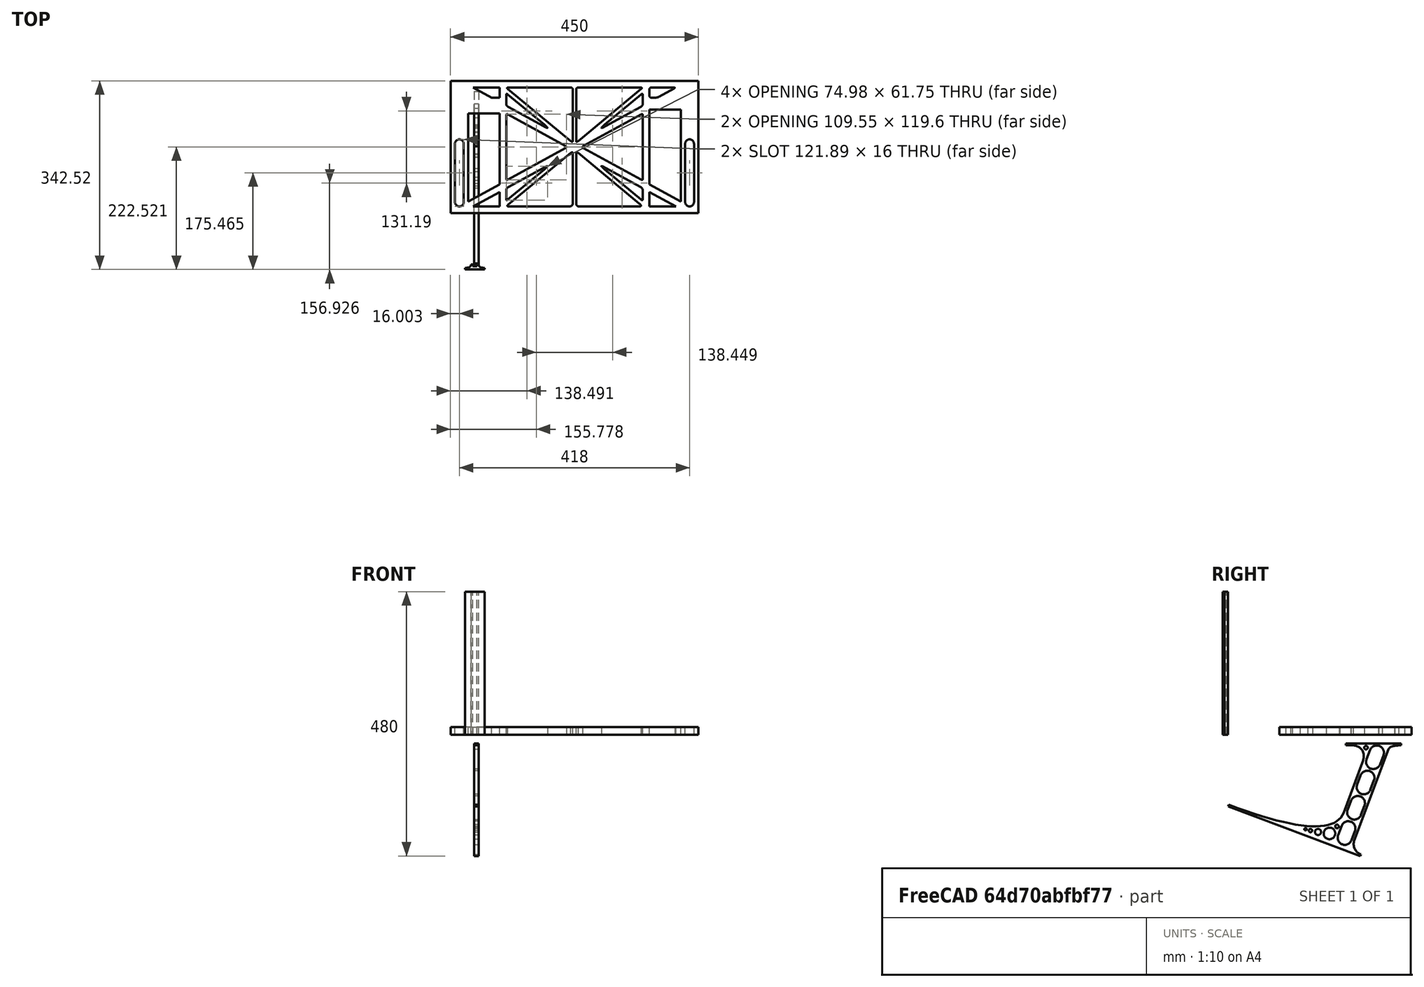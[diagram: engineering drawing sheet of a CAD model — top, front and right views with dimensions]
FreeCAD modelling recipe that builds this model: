
FCSTD DOCUMENT  (FreeCAD 0.19R0.19.2)
Label: laptopStand101
License: All rights reserved
LicenseURL: http://en.wikipedia.org/wiki/All_rights_reserved
objects: Sketcher::SketchObject×3, Part::Extrusion×3
note: 6 computed .brp shape members not serialized (recipe doc carries the construction recipe); baked Part::Feature solids carry a one-line shape summary decoded from their .brp

FEATURE [Sketcher::SketchObject] Sketch
  FullyConstrained = false
  sketch-geometry (276):
    g0: LineSegment StartX=-10.9272 StartY=-82.7794 StartZ=0 EndX=46.0728 EndY=-51.4823 EndZ=0
    g1: LineSegment StartX=366.073 StartY=-91.7794 StartZ=0 EndX=318.073 EndY=-65.424 EndZ=0
    g2: LineSegment StartX=-10.9272 StartY=77.3346 StartZ=0 EndX=-10.9272 EndY=-82.7794 EndZ=0
    g3: LineSegment StartX=375.073 StartY=-82.7794 StartZ=0 EndX=375.073 EndY=83.9235 EndZ=0
    g4: LineSegment StartX=-1.92719 StartY=-91.7794 StartZ=0 EndX=46.0728 EndY=-91.7794 EndZ=0
    g5: LineSegment StartX=318.073 StartY=83.9235 StartZ=0 EndX=318.073 EndY=-51.4823 EndZ=0
    g6: LineSegment StartX=318.073 StartY=-51.4823 StartZ=0 EndX=375.073 EndY=-82.7794 EndZ=0
    g7: LineSegment StartX=318.073 StartY=-65.424 StartZ=0 EndX=318.073 EndY=-91.7794 EndZ=0
    g8: LineSegment StartX=318.073 StartY=-91.7794 StartZ=0 EndX=366.073 EndY=-91.7794 EndZ=0
    g9: LineSegment StartX=46.0728 StartY=-65.424 StartZ=0 EndX=-1.92719 EndY=-91.7794 EndZ=0
    g10: LineSegment StartX=46.0728 StartY=-65.424 StartZ=0 EndX=46.0728 EndY=-91.7794 EndZ=0
    g11: LineSegment StartX=46.0728 StartY=77.3346 StartZ=0 EndX=46.0728 EndY=-51.4823 EndZ=0
    g12: LineSegment StartX=-42.9272 StartY=136.221 StartZ=0 EndX=-42.9272 EndY=-103.779 EndZ=0
    g13: LineSegment StartX=407.073 StartY=136.221 StartZ=0 EndX=407.073 EndY=-103.779 EndZ=0
    g14: ArcOfCircle CenterX=-26.9272 CenterY=22.1087 CenterZ=0 NormalX=0 NormalY=0 NormalZ=1 AngleXU=0 Radius=8 StartAngle=1e-16 EndAngle=3.14159
    g15: ArcOfCircle CenterX=-26.9272 CenterY=-83.7794 CenterZ=0 NormalX=0 NormalY=0 NormalZ=1 AngleXU=0 Radius=8 StartAngle=3.14159 EndAngle=6.28319
    g16: LineSegment StartX=-34.9272 StartY=22.1087 StartZ=0 EndX=-34.9272 EndY=-83.7794 EndZ=0
    g17: LineSegment StartX=-18.9272 StartY=22.1087 StartZ=0 EndX=-18.9272 EndY=-83.7794 EndZ=0
    g18: ArcOfCircle CenterX=391.073 CenterY=22.1087 CenterZ=0 NormalX=0 NormalY=0 NormalZ=1 AngleXU=0 Radius=8 StartAngle=-4.4e-15 EndAngle=3.14159
    g19: LineSegment StartX=399.073 StartY=22.1087 StartZ=0 EndX=399.073 EndY=-83.7794 EndZ=0
    g20: LineSegment StartX=383.073 StartY=22.1087 StartZ=0 EndX=383.073 EndY=-83.7794 EndZ=0
    g21: ArcOfCircle CenterX=391.073 CenterY=-83.7794 CenterZ=0 NormalX=0 NormalY=0 NormalZ=1 AngleXU=0 Radius=8 StartAngle=3.14159 EndAngle=6.28319
    g22: Circle CenterX=175.022 CenterY=27.0628 CenterZ=0 NormalX=0 NormalY=0 NormalZ=1 AngleXU=0 Radius=1
    g23: Circle CenterX=179.022 CenterY=24.8665 CenterZ=0 NormalX=0 NormalY=0 NormalZ=1 AngleXU=0 Radius=1
    g24: Circle CenterX=179.022 CenterY=27.0628 CenterZ=0 NormalX=0 NormalY=0 NormalZ=1 AngleXU=0 Radius=1
    g25: BSplineCurve PolesCount=3 KnotsCount=2 Degree=2 IsPeriodic=0
    g26: GeomPoint X=175.022 Y=27.0628 Z=0
    g27: GeomPoint X=179.022 Y=27.0628 Z=0
    g28: Circle CenterX=189.124 CenterY=27.0628 CenterZ=0 NormalX=0 NormalY=0 NormalZ=1 AngleXU=0 Radius=1
    g29: Circle CenterX=185.124 CenterY=24.8665 CenterZ=0 NormalX=0 NormalY=0 NormalZ=1 AngleXU=0 Radius=1
    g30: Circle CenterX=185.124 CenterY=27.0628 CenterZ=0 NormalX=0 NormalY=0 NormalZ=1 AngleXU=0 Radius=1
    g31: BSplineCurve PolesCount=3 KnotsCount=2 Degree=2 IsPeriodic=0
    g32: GeomPoint X=189.124 Y=27.0628 Z=0
    g33: GeomPoint X=185.124 Y=27.0628 Z=0
    g34: Circle CenterX=175.022 CenterY=5.37834 CenterZ=0 NormalX=0 NormalY=0 NormalZ=1 AngleXU=0 Radius=1
    g35: Circle CenterX=179.022 CenterY=7.57463 CenterZ=0 NormalX=0 NormalY=0 NormalZ=1 AngleXU=0 Radius=1
    g36: Circle CenterX=179.022 CenterY=5.34704 CenterZ=0 NormalX=0 NormalY=0 NormalZ=1 AngleXU=0 Radius=1
    g37: BSplineCurve PolesCount=3 KnotsCount=2 Degree=2 IsPeriodic=0
    g38: GeomPoint X=175.022 Y=5.37834 Z=0
    g39: GeomPoint X=179.022 Y=5.34704 Z=0
    g40: Circle CenterX=189.124 CenterY=5.37834 CenterZ=0 NormalX=0 NormalY=0 NormalZ=1 AngleXU=0 Radius=1
    g41: Circle CenterX=185.124 CenterY=7.57463 CenterZ=0 NormalX=0 NormalY=0 NormalZ=1 AngleXU=0 Radius=1
    g42: Circle CenterX=185.124 CenterY=5.34704 CenterZ=0 NormalX=0 NormalY=0 NormalZ=1 AngleXU=0 Radius=1
    g43: BSplineCurve PolesCount=3 KnotsCount=2 Degree=2 IsPeriodic=0
    g44: GeomPoint X=189.124 Y=5.37834 Z=0
    g45: GeomPoint X=185.124 Y=5.34704 Z=0
    g46: Circle CenterX=165.871 CenterY=18.1458 CenterZ=0 NormalX=0 NormalY=0 NormalZ=1 AngleXU=0 Radius=1
    g47: Circle CenterX=169.377 CenterY=16.2206 CenterZ=0 NormalX=0 NormalY=0 NormalZ=1 AngleXU=0 Radius=1
    g48: Circle CenterX=165.871 CenterY=14.2954 CenterZ=0 NormalX=0 NormalY=0 NormalZ=1 AngleXU=0 Radius=1
    g49: BSplineCurve PolesCount=3 KnotsCount=2 Degree=2 IsPeriodic=0
    g50: GeomPoint X=165.871 Y=18.1458 Z=0
    g51: GeomPoint X=165.871 Y=14.2954 Z=0
    g52: Circle CenterX=198.275 CenterY=18.1458 CenterZ=0 NormalX=0 NormalY=0 NormalZ=1 AngleXU=0 Radius=1
    g53: Circle CenterX=194.768 CenterY=16.2206 CenterZ=0 NormalX=0 NormalY=0 NormalZ=1 AngleXU=0 Radius=1
    g54: Circle CenterX=198.275 CenterY=14.2954 CenterZ=0 NormalX=0 NormalY=0 NormalZ=1 AngleXU=0 Radius=1
    g55: BSplineCurve PolesCount=3 KnotsCount=2 Degree=2 IsPeriodic=0
    g56: GeomPoint X=198.275 Y=18.1458 Z=0
    g57: GeomPoint X=198.275 Y=14.2954 Z=0
    g58: LineSegment StartX=407.073 StartY=-103.779 StartZ=0 EndX=-42.9272 EndY=-103.779 EndZ=0
    g59: LineSegment StartX=407.073 StartY=136.221 StartZ=0 EndX=-42.9272 EndY=136.221 EndZ=0
    g60: LineSegment StartX=46.0728 StartY=77.3346 StartZ=0 EndX=-10.9272 EndY=77.3346 EndZ=0
    g61: LineSegment StartX=46.0728 StartY=105.865 StartZ=0 EndX=31.5028 EndY=105.865 EndZ=0
    g62: LineSegment StartX=46.0728 StartY=124.221 StartZ=0 EndX=46.0728 EndY=105.865 EndZ=0
    g63: LineSegment StartX=-1.92719 StartY=124.221 StartZ=0 EndX=31.5028 EndY=105.865 EndZ=0
    g64: LineSegment StartX=46.0728 StartY=124.221 StartZ=0 EndX=-1.92719 EndY=124.221 EndZ=0
    g65: LineSegment StartX=318.073 StartY=83.9235 StartZ=0 EndX=375.073 EndY=83.9235 EndZ=0
    g66: Circle CenterX=125.607 CenterY=54.1951 CenterZ=0 NormalX=0 NormalY=0 NormalZ=1 AngleXU=0 Radius=1
    g67: Circle CenterX=139.632 CenterY=46.4944 CenterZ=0 NormalX=0 NormalY=0 NormalZ=1 AngleXU=0 Radius=1
    g68: Circle CenterX=127.326 CenterY=56.7187 CenterZ=0 NormalX=0 NormalY=0 NormalZ=1 AngleXU=0 Radius=1
    g69: BSplineCurve PolesCount=3 KnotsCount=2 Degree=2 IsPeriodic=0
    g70: GeomPoint X=125.607 Y=54.1951 Z=0
    g71: GeomPoint X=127.326 Y=56.7187 Z=0
    g72: Circle CenterX=236.821 CenterY=56.7187 CenterZ=0 NormalX=0 NormalY=0 NormalZ=1 AngleXU=0 Radius=1
    g73: Circle CenterX=224.513 CenterY=46.4944 CenterZ=0 NormalX=0 NormalY=0 NormalZ=1 AngleXU=0 Radius=1
    g74: Circle CenterX=238.538 CenterY=54.1951 CenterZ=0 NormalX=0 NormalY=0 NormalZ=1 AngleXU=0 Radius=1
    g75: BSplineCurve PolesCount=3 KnotsCount=2 Degree=2 IsPeriodic=0
    g76: GeomPoint X=236.821 Y=56.7187 Z=0
    g77: GeomPoint X=238.538 Y=54.1951 Z=0
    g78: Circle CenterX=238.538 CenterY=-21.7539 CenterZ=0 NormalX=0 NormalY=0 NormalZ=1 AngleXU=0 Radius=1
    g79: Circle CenterX=224.513 CenterY=-14.0532 CenterZ=0 NormalX=0 NormalY=0 NormalZ=1 AngleXU=0 Radius=1
    g80: Circle CenterX=236.821 CenterY=-24.2775 CenterZ=0 NormalX=0 NormalY=0 NormalZ=1 AngleXU=0 Radius=1
    g81: BSplineCurve PolesCount=3 KnotsCount=2 Degree=2 IsPeriodic=0
    g82: GeomPoint X=238.538 Y=-21.7539 Z=0
    g83: GeomPoint X=236.821 Y=-24.2775 Z=0
    g84: Circle CenterX=125.607 CenterY=-21.7539 CenterZ=0 NormalX=0 NormalY=0 NormalZ=1 AngleXU=0 Radius=1
    g85: Circle CenterX=139.632 CenterY=-14.0532 CenterZ=0 NormalX=0 NormalY=0 NormalZ=1 AngleXU=0 Radius=1
    g86: Circle CenterX=127.325 CenterY=-24.2775 CenterZ=0 NormalX=0 NormalY=0 NormalZ=1 AngleXU=0 Radius=1
    g87: BSplineCurve PolesCount=3 KnotsCount=2 Degree=2 IsPeriodic=0
    g88: GeomPoint X=125.607 Y=-21.7539 Z=0
    g89: GeomPoint X=127.325 Y=-24.2775 Z=0
    g90: Circle CenterX=302.996 CenterY=111.695 CenterZ=0 NormalX=0 NormalY=0 NormalZ=1 AngleXU=0 Radius=1
    g91: Circle CenterX=306.073 CenterY=114.251 CenterZ=0 NormalX=0 NormalY=0 NormalZ=1 AngleXU=0 Radius=1
    g92: Circle CenterX=306.073 CenterY=110.251 CenterZ=0 NormalX=0 NormalY=0 NormalZ=1 AngleXU=0 Radius=1
    g93: BSplineCurve PolesCount=3 KnotsCount=2 Degree=2 IsPeriodic=0
    g94: GeomPoint X=302.996 Y=111.695 Z=0
    g95: GeomPoint X=306.073 Y=110.251 Z=0
    g96: Circle CenterX=306.073 CenterY=95.2763 CenterZ=0 NormalX=0 NormalY=0 NormalZ=1 AngleXU=0 Radius=1
    g97: Circle CenterX=306.073 CenterY=91.2763 CenterZ=0 NormalX=0 NormalY=0 NormalZ=1 AngleXU=0 Radius=1
    g98: Circle CenterX=302.567 CenterY=89.3511 CenterZ=0 NormalX=0 NormalY=0 NormalZ=1 AngleXU=0 Radius=1
    g99: BSplineCurve PolesCount=3 KnotsCount=2 Degree=2 IsPeriodic=0
    g100: GeomPoint X=306.073 Y=95.2763 Z=0
    g101: GeomPoint X=302.567 Y=89.3511 Z=0
    g102: LineSegment StartX=306.073 StartY=110.251 StartZ=0 EndX=306.073 EndY=95.2763 EndZ=0
    g103: LineSegment StartX=302.996 StartY=111.695 StartZ=0 EndX=236.821 EndY=56.7187 EndZ=0
    g104: LineSegment StartX=238.538 StartY=54.1951 StartZ=0 EndX=302.567 EndY=89.3511 EndZ=0
    g105: Circle CenterX=61.1496 CenterY=111.695 CenterZ=0 NormalX=0 NormalY=0 NormalZ=1 AngleXU=0 Radius=1
    g106: Circle CenterX=58.0728 CenterY=114.251 CenterZ=0 NormalX=0 NormalY=0 NormalZ=1 AngleXU=0 Radius=1
    g107: Circle CenterX=58.0728 CenterY=110.251 CenterZ=0 NormalX=0 NormalY=0 NormalZ=1 AngleXU=0 Radius=1
    g108: BSplineCurve PolesCount=3 KnotsCount=2 Degree=2 IsPeriodic=0
    g109: GeomPoint X=61.1496 Y=111.695 Z=0
    g110: GeomPoint X=58.0728 Y=110.251 Z=0
    g111: Circle CenterX=61.5791 CenterY=89.3511 CenterZ=0 NormalX=0 NormalY=0 NormalZ=1 AngleXU=0 Radius=1
    g112: Circle CenterX=58.0728 CenterY=91.2763 CenterZ=0 NormalX=0 NormalY=0 NormalZ=1 AngleXU=0 Radius=1
    g113: Circle CenterX=58.0728 CenterY=95.2763 CenterZ=0 NormalX=0 NormalY=0 NormalZ=1 AngleXU=0 Radius=1
    g114: BSplineCurve PolesCount=3 KnotsCount=2 Degree=2 IsPeriodic=0
    g115: GeomPoint X=61.5791 Y=89.3511 Z=0
    g116: GeomPoint X=58.0728 Y=95.2763 Z=0
    g117: LineSegment StartX=58.0728 StartY=110.251 StartZ=0 EndX=58.0728 EndY=95.2763 EndZ=0
    g118: LineSegment StartX=61.1496 StartY=111.695 StartZ=0 EndX=127.326 EndY=56.7187 EndZ=0
    g119: LineSegment StartX=125.607 StartY=54.1951 StartZ=0 EndX=61.5791 EndY=89.3511 EndZ=0
    g120: Circle CenterX=61.5791 CenterY=-56.9099 CenterZ=0 NormalX=0 NormalY=0 NormalZ=1 AngleXU=0 Radius=1
    g121: Circle CenterX=58.0728 CenterY=-58.8351 CenterZ=0 NormalX=0 NormalY=0 NormalZ=1 AngleXU=0 Radius=1
    g122: Circle CenterX=58.0728 CenterY=-62.8351 CenterZ=0 NormalX=0 NormalY=0 NormalZ=1 AngleXU=0 Radius=1
    g123: BSplineCurve PolesCount=3 KnotsCount=2 Degree=2 IsPeriodic=0
    g124: GeomPoint X=61.5791 Y=-56.9099 Z=0
    g125: GeomPoint X=58.0728 Y=-62.8351 Z=0
    g126: Circle CenterX=58.0728 CenterY=-77.8102 CenterZ=0 NormalX=0 NormalY=0 NormalZ=1 AngleXU=0 Radius=1
    g127: Circle CenterX=58.0728 CenterY=-81.8102 CenterZ=0 NormalX=0 NormalY=0 NormalZ=1 AngleXU=0 Radius=1
    g128: Circle CenterX=61.1496 CenterY=-79.2541 CenterZ=0 NormalX=0 NormalY=0 NormalZ=1 AngleXU=0 Radius=1
    g129: BSplineCurve PolesCount=3 KnotsCount=2 Degree=2 IsPeriodic=0
    g130: GeomPoint X=58.0728 Y=-77.8102 Z=0
    g131: GeomPoint X=61.1496 Y=-79.2541 Z=0
    g132: LineSegment StartX=58.0728 StartY=-62.8351 StartZ=0 EndX=58.0728 EndY=-77.8102 EndZ=0
    g133: LineSegment StartX=61.1496 StartY=-79.2541 StartZ=0 EndX=127.325 EndY=-24.2775 EndZ=0
    g134: LineSegment StartX=125.607 StartY=-21.7539 StartZ=0 EndX=61.5791 EndY=-56.9099 EndZ=0
    g135: Circle CenterX=302.567 CenterY=-56.9099 CenterZ=0 NormalX=0 NormalY=0 NormalZ=1 AngleXU=0 Radius=1
    g136: Circle CenterX=306.073 CenterY=-58.8351 CenterZ=0 NormalX=0 NormalY=0 NormalZ=1 AngleXU=0 Radius=1
    g137: Circle CenterX=306.073 CenterY=-62.8351 CenterZ=0 NormalX=0 NormalY=0 NormalZ=1 AngleXU=0 Radius=1
    g138: BSplineCurve PolesCount=3 KnotsCount=2 Degree=2 IsPeriodic=0
    g139: GeomPoint X=302.567 Y=-56.9099 Z=0
    g140: GeomPoint X=306.073 Y=-62.8351 Z=0
    g141: Circle CenterX=302.996 CenterY=-79.2541 CenterZ=0 NormalX=0 NormalY=0 NormalZ=1 AngleXU=0 Radius=1
    g142: Circle CenterX=306.073 CenterY=-81.8102 CenterZ=0 NormalX=0 NormalY=0 NormalZ=1 AngleXU=0 Radius=1
    g143: Circle CenterX=306.073 CenterY=-77.8102 CenterZ=0 NormalX=0 NormalY=0 NormalZ=1 AngleXU=0 Radius=1
    g144: BSplineCurve PolesCount=3 KnotsCount=2 Degree=2 IsPeriodic=0
    g145: GeomPoint X=302.996 Y=-79.2541 Z=0
    g146: GeomPoint X=306.073 Y=-77.8102 Z=0
    g147: LineSegment StartX=306.073 StartY=-62.8351 StartZ=0 EndX=306.073 EndY=-77.8102 EndZ=0
    g148: LineSegment StartX=302.996 StartY=-79.2541 StartZ=0 EndX=236.821 EndY=-24.2775 EndZ=0
    g149: LineSegment StartX=238.538 StartY=-21.7539 StartZ=0 EndX=302.567 EndY=-56.9099 EndZ=0
    g150: Circle CenterX=61.6457 CenterY=-88.8112 CenterZ=0 NormalX=0 NormalY=0 NormalZ=1 AngleXU=0 Radius=1
    g151: Circle CenterX=58.0728 CenterY=-91.7794 CenterZ=0 NormalX=0 NormalY=0 NormalZ=1 AngleXU=0 Radius=1
    g152: Circle CenterX=63.9135 CenterY=-91.7794 CenterZ=0 NormalX=0 NormalY=0 NormalZ=1 AngleXU=0 Radius=1
    g153: BSplineCurve PolesCount=3 KnotsCount=2 Degree=2 IsPeriodic=0
    g154: GeomPoint X=61.6457 Y=-88.8112 Z=0
    g155: GeomPoint X=63.9135 Y=-91.7794 Z=0
    g156: Circle CenterX=179.022 CenterY=-85.8163 CenterZ=0 NormalX=0 NormalY=0 NormalZ=1 AngleXU=0 Radius=1
    g157: Circle CenterX=179.022 CenterY=-91.7794 CenterZ=0 NormalX=0 NormalY=0 NormalZ=1 AngleXU=0 Radius=1
    g158: Circle CenterX=171.895 CenterY=-91.7794 CenterZ=0 NormalX=0 NormalY=0 NormalZ=1 AngleXU=0 Radius=1
    g159: BSplineCurve PolesCount=3 KnotsCount=2 Degree=2 IsPeriodic=0
    g160: GeomPoint X=179.022 Y=-85.8163 Z=0
    g161: GeomPoint X=171.895 Y=-91.7794 Z=0
    g162: Circle CenterX=185.124 CenterY=-86.2028 CenterZ=0 NormalX=0 NormalY=0 NormalZ=1 AngleXU=0 Radius=1
    g163: Circle CenterX=185.124 CenterY=-91.7794 CenterZ=0 NormalX=0 NormalY=0 NormalZ=1 AngleXU=0 Radius=1
    g164: Circle CenterX=191.747 CenterY=-91.7794 CenterZ=0 NormalX=0 NormalY=0 NormalZ=1 AngleXU=0 Radius=1
    g165: BSplineCurve PolesCount=3 KnotsCount=2 Degree=2 IsPeriodic=0
    g166: GeomPoint X=185.124 Y=-86.2028 Z=0
    g167: GeomPoint X=191.747 Y=-91.7794 Z=0
    g168: Circle CenterX=299.888 CenterY=-86.6413 CenterZ=0 NormalX=0 NormalY=0 NormalZ=1 AngleXU=0 Radius=1
    g169: Circle CenterX=306.073 CenterY=-91.7794 CenterZ=0 NormalX=0 NormalY=0 NormalZ=1 AngleXU=0 Radius=1
    g170: Circle CenterX=298.776 CenterY=-91.7794 CenterZ=0 NormalX=0 NormalY=0 NormalZ=1 AngleXU=0 Radius=1
    g171: BSplineCurve PolesCount=3 KnotsCount=2 Degree=2 IsPeriodic=0
    g172: GeomPoint X=299.888 Y=-86.6413 Z=0
    g173: GeomPoint X=298.776 Y=-91.7794 Z=0
    g174: LineSegment StartX=189.124 StartY=5.37834 StartZ=0 EndX=299.888 EndY=-86.6413 EndZ=0
    g175: LineSegment StartX=298.776 StartY=-91.7794 StartZ=0 EndX=191.747 EndY=-91.7794 EndZ=0
    g176: LineSegment StartX=185.124 StartY=-86.2028 StartZ=0 EndX=185.124 EndY=5.34704 EndZ=0
    g177: LineSegment StartX=179.022 StartY=5.34704 StartZ=0 EndX=179.022 EndY=-85.8163 EndZ=0
    g178: LineSegment StartX=171.895 StartY=-91.7794 StartZ=0 EndX=63.9135 EndY=-91.7794 EndZ=0
    g179: LineSegment StartX=61.6457 StartY=-88.8112 StartZ=0 EndX=175.022 EndY=5.37834 EndZ=0
    g180: Circle CenterX=302.073 CenterY=124.221 CenterZ=0 NormalX=0 NormalY=0 NormalZ=1 AngleXU=0 Radius=1
    g181: Circle CenterX=306.073 CenterY=124.221 CenterZ=0 NormalX=0 NormalY=0 NormalZ=1 AngleXU=0 Radius=1
    g182: Circle CenterX=302.996 CenterY=121.665 CenterZ=0 NormalX=0 NormalY=0 NormalZ=1 AngleXU=0 Radius=1
    g183: BSplineCurve PolesCount=3 KnotsCount=2 Degree=2 IsPeriodic=0
    g184: GeomPoint X=302.073 Y=124.221 Z=0
    g185: GeomPoint X=302.996 Y=121.665 Z=0
    g186: Circle CenterX=189.124 CenterY=124.221 CenterZ=0 NormalX=0 NormalY=0 NormalZ=1 AngleXU=0 Radius=1
    g187: Circle CenterX=185.124 CenterY=124.221 CenterZ=0 NormalX=0 NormalY=0 NormalZ=1 AngleXU=0 Radius=1
    g188: Circle CenterX=185.124 CenterY=120.221 CenterZ=0 NormalX=0 NormalY=0 NormalZ=1 AngleXU=0 Radius=1
    g189: BSplineCurve PolesCount=3 KnotsCount=2 Degree=2 IsPeriodic=0
    g190: GeomPoint X=189.124 Y=124.221 Z=0
    g191: GeomPoint X=185.124 Y=120.221 Z=0
    g192: Circle CenterX=175.022 CenterY=124.221 CenterZ=0 NormalX=0 NormalY=0 NormalZ=1 AngleXU=0 Radius=1
    g193: Circle CenterX=179.022 CenterY=124.221 CenterZ=0 NormalX=0 NormalY=0 NormalZ=1 AngleXU=0 Radius=1
    g194: Circle CenterX=179.022 CenterY=120.221 CenterZ=0 NormalX=0 NormalY=0 NormalZ=1 AngleXU=0 Radius=1
    g195: BSplineCurve PolesCount=3 KnotsCount=2 Degree=2 IsPeriodic=0
    g196: GeomPoint X=175.022 Y=124.221 Z=0
    g197: GeomPoint X=179.022 Y=120.221 Z=0
    g198: Circle CenterX=62.0728 CenterY=124.221 CenterZ=0 NormalX=0 NormalY=0 NormalZ=1 AngleXU=0 Radius=1
    g199: Circle CenterX=58.0728 CenterY=124.221 CenterZ=0 NormalX=0 NormalY=0 NormalZ=1 AngleXU=0 Radius=1
    g200: Circle CenterX=61.1496 CenterY=121.665 CenterZ=0 NormalX=0 NormalY=0 NormalZ=1 AngleXU=0 Radius=1
    g201: BSplineCurve PolesCount=3 KnotsCount=2 Degree=2 IsPeriodic=0
    g202: GeomPoint X=62.0728 Y=124.221 Z=0
    g203: GeomPoint X=61.1496 Y=121.665 Z=0
    g204: LineSegment StartX=62.0728 StartY=124.221 StartZ=0 EndX=175.022 EndY=124.221 EndZ=0
    g205: LineSegment StartX=179.022 StartY=120.221 StartZ=0 EndX=179.022 EndY=27.0628 EndZ=0
    g206: LineSegment StartX=185.124 StartY=27.0628 StartZ=0 EndX=185.124 EndY=120.221 EndZ=0
    g207: LineSegment StartX=189.124 StartY=124.221 StartZ=0 EndX=302.073 EndY=124.221 EndZ=0
    g208: LineSegment StartX=302.996 StartY=121.665 StartZ=0 EndX=189.124 EndY=27.0628 EndZ=0
    g209: LineSegment StartX=175.022 StartY=27.0628 StartZ=0 EndX=61.1496 EndY=121.665 EndZ=0
    g210: Circle CenterX=61.5791 CenterY=75.4095 CenterZ=0 NormalX=0 NormalY=0 NormalZ=1 AngleXU=0 Radius=1
    g211: Circle CenterX=58.0728 CenterY=77.3346 CenterZ=0 NormalX=0 NormalY=0 NormalZ=1 AngleXU=0 Radius=1
    g212: Circle CenterX=58.0728 CenterY=73.3346 CenterZ=0 NormalX=0 NormalY=0 NormalZ=1 AngleXU=0 Radius=1
    g213: BSplineCurve PolesCount=3 KnotsCount=2 Degree=2 IsPeriodic=0
    g214: GeomPoint X=61.5791 Y=75.4095 Z=0
    g215: GeomPoint X=58.0728 Y=73.3346 Z=0
    g216: Circle CenterX=58.0728 CenterY=-40.8935 CenterZ=0 NormalX=0 NormalY=0 NormalZ=1 AngleXU=0 Radius=1
    g217: Circle CenterX=58.0728 CenterY=-44.8935 CenterZ=0 NormalX=0 NormalY=0 NormalZ=1 AngleXU=0 Radius=1
    g218: Circle CenterX=61.5791 CenterY=-42.9683 CenterZ=0 NormalX=0 NormalY=0 NormalZ=1 AngleXU=0 Radius=1
    g219: BSplineCurve PolesCount=3 KnotsCount=2 Degree=2 IsPeriodic=0
    g220: GeomPoint X=58.0728 Y=-40.8935 Z=0
    g221: GeomPoint X=61.5791 Y=-42.9683 Z=0
    g222: LineSegment StartX=61.5791 StartY=-42.9683 StartZ=0 EndX=165.871 EndY=14.2954 EndZ=0
    g223: LineSegment StartX=165.871 StartY=18.1458 StartZ=0 EndX=61.5791 EndY=75.4095 EndZ=0
    g224: LineSegment StartX=58.0728 StartY=73.3346 StartZ=0 EndX=58.0728 EndY=-40.8935 EndZ=0
    g225: Circle CenterX=302.567 CenterY=-42.9683 CenterZ=0 NormalX=0 NormalY=0 NormalZ=1 AngleXU=0 Radius=1
    g226: Circle CenterX=306.073 CenterY=-44.8935 CenterZ=0 NormalX=0 NormalY=0 NormalZ=1 AngleXU=0 Radius=1
    g227: Circle CenterX=306.073 CenterY=-40.8935 CenterZ=0 NormalX=0 NormalY=0 NormalZ=1 AngleXU=0 Radius=1
    g228: BSplineCurve PolesCount=3 KnotsCount=2 Degree=2 IsPeriodic=0
    g229: GeomPoint X=302.567 Y=-42.9683 Z=0
    g230: GeomPoint X=306.073 Y=-40.8935 Z=0
    g231: Circle CenterX=306.073 CenterY=73.3346 CenterZ=0 NormalX=0 NormalY=0 NormalZ=1 AngleXU=0 Radius=1
    g232: Circle CenterX=306.073 CenterY=77.3346 CenterZ=0 NormalX=0 NormalY=0 NormalZ=1 AngleXU=0 Radius=1
    g233: Circle CenterX=302.567 CenterY=75.4095 CenterZ=0 NormalX=0 NormalY=0 NormalZ=1 AngleXU=0 Radius=1
    g234: BSplineCurve PolesCount=3 KnotsCount=2 Degree=2 IsPeriodic=0
    g235: GeomPoint X=306.073 Y=73.3346 Z=0
    g236: GeomPoint X=302.567 Y=75.4095 Z=0
    g237: LineSegment StartX=302.567 StartY=-42.9683 StartZ=0 EndX=198.275 EndY=14.2954 EndZ=0
    g238: LineSegment StartX=198.275 StartY=18.1458 StartZ=0 EndX=302.567 EndY=75.4095 EndZ=0
    g239: LineSegment StartX=306.073 StartY=73.3346 StartZ=0 EndX=306.073 EndY=-40.8935 EndZ=0
    g240: LineSegment StartX=322.073 StartY=105.865 StartZ=0 EndX=328.643 EndY=105.865 EndZ=0
    g241: LineSegment StartX=318.073 StartY=120.221 StartZ=0 EndX=318.073 EndY=109.865 EndZ=0
    g242: LineSegment StartX=336.157 StartY=107.779 StartZ=0 EndX=362.567 EndY=122.294 EndZ=0
    g243: Circle CenterX=362.073 CenterY=124.221 CenterZ=0 NormalX=0 NormalY=0 NormalZ=1 AngleXU=0 Radius=1
    g244: Circle CenterX=366.073 CenterY=124.221 CenterZ=0 NormalX=0 NormalY=0 NormalZ=1 AngleXU=0 Radius=1
    g245: Circle CenterX=362.567 CenterY=122.294 CenterZ=0 NormalX=0 NormalY=0 NormalZ=1 AngleXU=0 Radius=1
    g246: BSplineCurve PolesCount=3 KnotsCount=2 Degree=2 IsPeriodic=0
    g247: GeomPoint X=362.073 Y=124.221 Z=0
    g248: GeomPoint X=362.567 Y=122.294 Z=0
    g249: Circle CenterX=322.073 CenterY=124.221 CenterZ=0 NormalX=0 NormalY=0 NormalZ=1 AngleXU=0 Radius=1
    g250: Circle CenterX=318.073 CenterY=124.221 CenterZ=0 NormalX=0 NormalY=0 NormalZ=1 AngleXU=0 Radius=1
    g251: Circle CenterX=318.073 CenterY=120.221 CenterZ=0 NormalX=0 NormalY=0 NormalZ=1 AngleXU=0 Radius=1
    g252: BSplineCurve PolesCount=3 KnotsCount=2 Degree=2 IsPeriodic=0
    g253: GeomPoint X=322.073 Y=124.221 Z=0
    g254: GeomPoint X=318.073 Y=120.221 Z=0
    g255: Circle CenterX=322.073 CenterY=105.865 CenterZ=0 NormalX=0 NormalY=0 NormalZ=1 AngleXU=0 Radius=1
    g256: Circle CenterX=318.073 CenterY=105.865 CenterZ=0 NormalX=0 NormalY=0 NormalZ=1 AngleXU=0 Radius=1
    g257: Circle CenterX=318.073 CenterY=109.865 CenterZ=0 NormalX=0 NormalY=0 NormalZ=1 AngleXU=0 Radius=1
    g258: BSplineCurve PolesCount=3 KnotsCount=2 Degree=2 IsPeriodic=0
    g259: GeomPoint X=322.073 Y=105.865 Z=0
    g260: GeomPoint X=318.073 Y=109.865 Z=0
    g261: Circle CenterX=336.157 CenterY=107.779 CenterZ=0 NormalX=0 NormalY=0 NormalZ=1 AngleXU=0 Radius=1
    g262: Circle CenterX=332.651 CenterY=105.853 CenterZ=0 NormalX=0 NormalY=0 NormalZ=1 AngleXU=0 Radius=1
    g263: Circle CenterX=328.643 CenterY=105.865 CenterZ=0 NormalX=0 NormalY=0 NormalZ=1 AngleXU=0 Radius=1
    g264: BSplineCurve PolesCount=3 KnotsCount=2 Degree=2 IsPeriodic=0
    g265: GeomPoint X=336.157 Y=107.779 Z=0
    g266: GeomPoint X=328.643 Y=105.865 Z=0
    g267: LineSegment StartX=322.073 StartY=124.221 StartZ=0 EndX=362.073 EndY=124.221 EndZ=0
    g268: LineSegment StartX=319.373 StartY=85.0727 StartZ=0 EndX=323.373 EndY=85.0727 EndZ=0
    g269: LineSegment StartX=317.109 StartY=82.5747 StartZ=0 EndX=317.109 EndY=78.5747 EndZ=0
    g270: LineSegment StartX=374.232 StartY=84.6841 StartZ=0 EndX=370.232 EndY=84.6841 EndZ=0
    g271: LineSegment StartX=376.298 StartY=83.163 StartZ=0 EndX=376.298 EndY=79.163 EndZ=0
    g272: LineSegment StartX=375.914 StartY=-82.2546 StartZ=0 EndX=375.914 EndY=-78.2546 EndZ=0
    g273: LineSegment StartX=373.008 StartY=-82.8971 StartZ=0 EndX=369.501 EndY=-80.9719 EndZ=0
    g274: LineSegment StartX=319.637 StartY=-54.0192 StartZ=0 EndX=323.143 EndY=-55.9444 EndZ=0
    g275: LineSegment StartX=316.982 StartY=-47.6475 StartZ=0 EndX=316.982 EndY=-43.6475 EndZ=0
  constraints (465):
    c: Horizontal(g4)
    c: Coincident(g5,g6)
    c: Coincident(g7,g1)
    c: Tangent(g5,g7)
    c: Coincident(g10,g9)
    c: Coincident(g0,g11)
    c: Block(g6)
    c: Block(g3)
    c: Block(g1)
    c: Block(g7)
    c: Block(g10)
    c: Block(g9)
    c: Block(g0)
    c: Block(g2)
    c: Block(g8)
    c: Block(g4)
    c: Vertical(g12)
    c: Vertical(g13)
    c: Block(g13)
    c: Block(g12)
    c: Tangent(g14,g17) = 1.5708
    c: Tangent(g14,g16) = -1.5708
    c: Tangent(g16,g15) = -1.5708
    c: Tangent(g17,g15) = 1.5708
    c: Vertical(g16)
    c: Equal(g14,g15)
    c: Block(g17)
    c: Block(g16)
    c: Tangent(g18,g19) = 1.5708
    c: Tangent(g19,g21) = 1.5708
    c: Equal(g18,g21)
    c: Coincident(g20,g18)
    c: Coincident(g20,g21)
    c: Block(g19)
    c: Block(g20)
    c: Weight(g22) = 1
    c: Equal(g22,g23)
    c: Equal(g22,g24)
    c: InternalAlignment(g22,g25)
    c: InternalAlignment(g23,g25)
    c: InternalAlignment(g24,g25)
    c: InternalAlignment(g26,g25)
    c: InternalAlignment(g27,g25)
    c: Weight(g28) = 1
    c: Equal(g28,g29)
    c: Equal(g28,g30)
    c: InternalAlignment(g28,g31)
    c: InternalAlignment(g29,g31)
    c: InternalAlignment(g30,g31)
    c: InternalAlignment(g32,g31)
    c: InternalAlignment(g33,g31)
    c: Block(g31)
    c: Block(g25)
    c: Weight(g34) = 1
    c: Equal(g34,g35)
    c: Equal(g34,g36)
    c: InternalAlignment(g34,g37)
    c: InternalAlignment(g35,g37)
    c: InternalAlignment(g36,g37)
    c: InternalAlignment(g38,g37)
    c: InternalAlignment(g39,g37)
    c: Weight(g40) = 1
    c: Equal(g40,g41)
    c: Equal(g40,g42)
    c: InternalAlignment(g40,g43)
    c: InternalAlignment(g41,g43)
    c: InternalAlignment(g42,g43)
    c: InternalAlignment(g44,g43)
    c: InternalAlignment(g45,g43)
    c: Block(g43)
    c: Block(g37)
    c: Weight(g46) = 1
    c: Equal(g46,g47)
    c: Equal(g46,g48)
    c: InternalAlignment(g46,g49)
    c: InternalAlignment(g47,g49)
    c: InternalAlignment(g48,g49)
    c: InternalAlignment(g50,g49)
    c: InternalAlignment(g51,g49)
    c: Weight(g52) = 1
    c: Equal(g52,g53)
    c: Equal(g52,g54)
    c: InternalAlignment(g52,g55)
    c: InternalAlignment(g53,g55)
    c: InternalAlignment(g54,g55)
    c: InternalAlignment(g56,g55)
    c: InternalAlignment(g57,g55)
    c: Block(g49)
    c: Block(g55)
    c: Coincident(g58,g13)
    c: Coincident(g58,g12)
    c: Horizontal(g58)
    c: Distance(g58) = 450
    c: Coincident(g59,g13)
    c: Coincident(g59,g12)
    c: Horizontal(g59)
    c: Horizontal(g60)
    c: Coincident(g11,g60)
    c: Horizontal(g61)
    c: Vertical(g62)
    c: Block(g62)
    c: Block(g61)
    c: Block(g60)
    c: Distance(g62) = 18.3554
    c: Coincident(g64,g62)
    c: Coincident(g64,g63)
    c: Horizontal(g64)
    c: Block(g64)
    c: Block(g63)
    c: Coincident(g61,g63)
    c: Coincident(g2,g60)
    c: Coincident(g65,g5)
    c: Horizontal(g65)
    c: Block(g65)
    c: Coincident(g3,g65)
    c: Weight(g66) = 1
    c: Equal(g66,g67)
    c: Equal(g66,g68)
    c: InternalAlignment(g66,g69)
    c: InternalAlignment(g67,g69)
    c: InternalAlignment(g68,g69)
    c: InternalAlignment(g70,g69)
    c: InternalAlignment(g71,g69)
    c: Block(g69)
    c: Weight(g72) = 1
    c: Equal(g72,g73)
    c: Equal(g72,g74)
    c: InternalAlignment(g72,g75)
    c: InternalAlignment(g73,g75)
    c: InternalAlignment(g74,g75)
    c: InternalAlignment(g76,g75)
    c: InternalAlignment(g77,g75)
    c: Block(g75)
    c: Weight(g78) = 1
    c: Equal(g78,g79)
    c: Equal(g78,g80)
    c: InternalAlignment(g78,g81)
    c: InternalAlignment(g79,g81)
    c: InternalAlignment(g80,g81)
    c: InternalAlignment(g82,g81)
    c: InternalAlignment(g83,g81)
    c: Block(g81)
    c: Weight(g84) = 1
    c: Equal(g84,g85)
    c: Equal(g84,g86)
    c: InternalAlignment(g84,g87)
    c: InternalAlignment(g85,g87)
    c: InternalAlignment(g86,g87)
    c: InternalAlignment(g88,g87)
    c: InternalAlignment(g89,g87)
    c: Block(g87)
    c: Weight(g90) = 1
    c: Equal(g90,g91)
    c: Equal(g90,g92)
    c: InternalAlignment(g90,g93)
    c: InternalAlignment(g91,g93)
    c: InternalAlignment(g92,g93)
    c: InternalAlignment(g94,g93)
    c: InternalAlignment(g95,g93)
    c: Weight(g96) = 1
    c: Equal(g96,g97)
    c: Equal(g96,g98)
    c: InternalAlignment(g96,g99)
    c: InternalAlignment(g97,g99)
    c: InternalAlignment(g98,g99)
    c: InternalAlignment(g100,g99)
    c: InternalAlignment(g101,g99)
    c: Block(g93)
    c: Block(g99)
    c: Coincident(g102,g93)
    c: Coincident(g102,g99)
    c: Vertical(g102)
    c: Coincident(g103,g93)
    c: Coincident(g103,g75)
    c: Coincident(g104,g75)
    c: Coincident(g104,g99)
    c: Weight(g105) = 1
    c: Equal(g105,g106)
    c: Equal(g105,g107)
    c: InternalAlignment(g105,g108)
    c: InternalAlignment(g106,g108)
    c: InternalAlignment(g107,g108)
    c: InternalAlignment(g109,g108)
    c: InternalAlignment(g110,g108)
    c: Weight(g111) = 1
    c: Equal(g111,g112)
    c: Equal(g111,g113)
    c: InternalAlignment(g111,g114)
    c: InternalAlignment(g112,g114)
    c: InternalAlignment(g113,g114)
    c: InternalAlignment(g115,g114)
    c: InternalAlignment(g116,g114)
    c: Block(g108)
    c: Block(g114)
    c: Coincident(g117,g108)
    c: Coincident(g117,g114)
    c: Vertical(g117)
    c: Coincident(g118,g108)
    c: Coincident(g118,g69)
    c: Coincident(g119,g69)
    c: Coincident(g119,g114)
    c: Weight(g120) = 1
    c: Equal(g120,g121)
    c: Equal(g120,g122)
    c: InternalAlignment(g120,g123)
    c: InternalAlignment(g121,g123)
    c: InternalAlignment(g122,g123)
    c: InternalAlignment(g124,g123)
    c: InternalAlignment(g125,g123)
    c: Weight(g126) = 1
    c: Equal(g126,g127)
    c: Equal(g126,g128)
    c: InternalAlignment(g126,g129)
    c: InternalAlignment(g127,g129)
    c: InternalAlignment(g128,g129)
    c: InternalAlignment(g130,g129)
    c: InternalAlignment(g131,g129)
    c: Block(g123)
    c: Block(g129)
    c: Coincident(g132,g123)
    c: Coincident(g132,g129)
    c: Vertical(g132)
    c: Coincident(g133,g129)
    c: Coincident(g133,g87)
    c: Coincident(g134,g87)
    c: Coincident(g134,g123)
    c: Weight(g135) = 1
    c: Equal(g135,g136)
    c: Equal(g135,g137)
    c: InternalAlignment(g135,g138)
    c: InternalAlignment(g136,g138)
    c: InternalAlignment(g137,g138)
    c: InternalAlignment(g139,g138)
    c: InternalAlignment(g140,g138)
    c: Weight(g141) = 1
    c: Equal(g141,g142)
    c: Equal(g141,g143)
    c: InternalAlignment(g141,g144)
    c: InternalAlignment(g142,g144)
    c: InternalAlignment(g143,g144)
    c: InternalAlignment(g145,g144)
    c: InternalAlignment(g146,g144)
    c: Block(g138)
    c: Block(g144)
    c: Coincident(g147,g138)
    c: Coincident(g147,g144)
    c: Vertical(g147)
    c: Coincident(g148,g144)
    c: Coincident(g148,g81)
    c: Coincident(g149,g81)
    c: Coincident(g149,g138)
    c: Weight(g150) = 1
    c: Equal(g150,g151)
    c: Equal(g150,g152)
    c: InternalAlignment(g150,g153)
    c: InternalAlignment(g151,g153)
    c: InternalAlignment(g152,g153)
    c: InternalAlignment(g154,g153)
    c: InternalAlignment(g155,g153)
    c: Weight(g156) = 1
    c: Equal(g156,g157)
    c: Equal(g156,g158)
    c: InternalAlignment(g156,g159)
    c: InternalAlignment(g157,g159)
    c: InternalAlignment(g158,g159)
    c: InternalAlignment(g160,g159)
    c: InternalAlignment(g161,g159)
    c: Weight(g162) = 1
    c: Equal(g162,g163)
    c: Equal(g162,g164)
    c: InternalAlignment(g162,g165)
    c: InternalAlignment(g163,g165)
    c: InternalAlignment(g164,g165)
    c: InternalAlignment(g166,g165)
    c: InternalAlignment(g167,g165)
    c: Weight(g168) = 1
    c: Equal(g168,g169)
    c: Equal(g168,g170)
    c: InternalAlignment(g168,g171)
    c: InternalAlignment(g169,g171)
    c: InternalAlignment(g170,g171)
    c: InternalAlignment(g172,g171)
    c: InternalAlignment(g173,g171)
    c: Block(g171)
    c: Block(g165)
    c: Block(g159)
    c: Block(g153)
    c: Coincident(g174,g43)
    c: Coincident(g174,g171)
    c: Coincident(g175,g171)
    c: Coincident(g175,g165)
    c: Horizontal(g175)
    c: Coincident(g176,g165)
    c: Coincident(g176,g43)
    c: Vertical(g176)
    c: Coincident(g177,g37)
    c: Coincident(g177,g159)
    c: Vertical(g177)
    c: Coincident(g178,g159)
    c: Coincident(g178,g153)
    c: Horizontal(g178)
    c: Coincident(g179,g153)
    c: Coincident(g179,g37)
    c: Weight(g180) = 1
    c: Equal(g180,g181)
    c: Equal(g180,g182)
    c: InternalAlignment(g180,g183)
    c: InternalAlignment(g181,g183)
    c: InternalAlignment(g182,g183)
    c: InternalAlignment(g184,g183)
    c: InternalAlignment(g185,g183)
    c: Weight(g186) = 1
    c: Equal(g186,g187)
    c: Equal(g186,g188)
    c: InternalAlignment(g186,g189)
    c: InternalAlignment(g187,g189)
    c: InternalAlignment(g188,g189)
    c: InternalAlignment(g190,g189)
    c: InternalAlignment(g191,g189)
    c: Weight(g192) = 1
    c: Equal(g192,g193)
    c: Equal(g192,g194)
    c: InternalAlignment(g192,g195)
    c: InternalAlignment(g193,g195)
    c: InternalAlignment(g194,g195)
    c: InternalAlignment(g196,g195)
    c: InternalAlignment(g197,g195)
    c: Weight(g198) = 1
    c: Equal(g198,g199)
    c: Equal(g198,g200)
    c: InternalAlignment(g198,g201)
    c: InternalAlignment(g199,g201)
    c: InternalAlignment(g200,g201)
    c: InternalAlignment(g202,g201)
    c: InternalAlignment(g203,g201)
    c: Block(g201)
    c: Block(g195)
    c: Block(g189)
    c: Block(g183)
    c: Coincident(g204,g201)
    c: Coincident(g204,g195)
    c: Horizontal(g204)
    c: Coincident(g205,g195)
    c: Coincident(g205,g25)
    c: Vertical(g205)
    c: Coincident(g206,g31)
    c: Coincident(g206,g189)
    c: Vertical(g206)
    c: Coincident(g207,g189)
    c: Coincident(g207,g183)
    c: Horizontal(g207)
    c: Coincident(g208,g183)
    c: Coincident(g208,g31)
    c: Coincident(g209,g25)
    c: Weight(g210) = 1
    c: Equal(g210,g211)
    c: Equal(g210,g212)
    c: InternalAlignment(g210,g213)
    c: InternalAlignment(g211,g213)
    c: InternalAlignment(g212,g213)
    c: InternalAlignment(g214,g213)
    c: InternalAlignment(g215,g213)
    c: Weight(g216) = 1
    c: Equal(g216,g217)
    c: Equal(g216,g218)
    c: InternalAlignment(g216,g219)
    c: InternalAlignment(g217,g219)
    c: InternalAlignment(g218,g219)
    c: InternalAlignment(g220,g219)
    c: InternalAlignment(g221,g219)
    c: Block(g219)
    c: Block(g213)
    c: Coincident(g222,g219)
    c: Coincident(g222,g49)
    c: Coincident(g223,g49)
    c: Coincident(g223,g213)
    c: Coincident(g224,g213)
    c: Coincident(g224,g219)
    c: Vertical(g224)
    c: Weight(g225) = 1
    c: Equal(g225,g226)
    c: Equal(g225,g227)
    c: InternalAlignment(g225,g228)
    c: InternalAlignment(g226,g228)
    c: InternalAlignment(g227,g228)
    c: InternalAlignment(g229,g228)
    c: InternalAlignment(g230,g228)
    c: Weight(g231) = 1
    c: Equal(g231,g232)
    c: Equal(g231,g233)
    c: InternalAlignment(g231,g234)
    c: InternalAlignment(g232,g234)
    c: InternalAlignment(g233,g234)
    c: InternalAlignment(g235,g234)
    c: InternalAlignment(g236,g234)
    c: Block(g234)
    c: Block(g228)
    c: Coincident(g237,g228)
    c: Coincident(g237,g55)
    c: Coincident(g238,g55)
    c: Coincident(g238,g234)
    c: Coincident(g239,g234)
    c: Coincident(g239,g228)
    c: Vertical(g239)
    c: Horizontal(g240)
    c: Block(g240)
    c: Vertical(g241)
    c: Block(g241)
    c: Block(g242)
    c: Weight(g243) = 1
    c: Equal(g243,g244)
    c: Equal(g243,g245)
    c: InternalAlignment(g243,g246)
    c: InternalAlignment(g244,g246)
    c: InternalAlignment(g245,g246)
    c: InternalAlignment(g247,g246)
    c: InternalAlignment(g248,g246)
    c: Weight(g249) = 1
    c: Equal(g249,g250)
    c: Equal(g249,g251)
    c: InternalAlignment(g249,g252)
    c: InternalAlignment(g250,g252)
    c: InternalAlignment(g251,g252)
    c: InternalAlignment(g253,g252)
    c: InternalAlignment(g254,g252)
    c: Weight(g255) = 1
    c: Equal(g255,g256)
    c: Equal(g255,g257)
    c: InternalAlignment(g255,g258)
    c: InternalAlignment(g256,g258)
    c: InternalAlignment(g257,g258)
    c: InternalAlignment(g259,g258)
    c: InternalAlignment(g260,g258)
    c: Weight(g261) = 1
    c: Equal(g261,g262)
    c: Equal(g261,g263)
    c: InternalAlignment(g261,g264)
    c: InternalAlignment(g262,g264)
    c: InternalAlignment(g263,g264)
    c: InternalAlignment(g265,g264)
    c: InternalAlignment(g266,g264)
    c: Block(g246)
    c: Block(g252)
    c: Block(g258)
    c: Block(g264)
    c: Coincident(g267,g252)
    c: Coincident(g267,g246)
    c: Horizontal(g267)
    c: Block(g209)
    c: Horizontal(g268)
    c: Vertical(g269)
    c: Horizontal(g270)
    c: Vertical(g271)
    c: Vertical(g272)
    c: Vertical(g275)
    c: Parallel(g6,g274)
    c: Parallel(g6,g273)
    c: Distance(g273) = 4
    c: Distance(g272) = 4
    c: Distance(g274) = 4
    c: Distance(g275) = 4
    c: Distance(g269) = 4
    c: Distance(g268) = 4
    c: Distance(g271) = 4
    c: Distance(g270) = 4
FEATURE [Sketcher::SketchObject] Sketch001
  FullyConstrained = true
  MapMode = 4
  Placement = pos=(0,0,0) rot=(0.57735,0.57735,0.57735;2.0944rad)
  Support = -> [Sketch]
  sketch-geometry (46):
    g0: BSplineCurve PolesCount=3 KnotsCount=2 Degree=2 IsPeriodic=0
    g1: ArcOfCircle CenterX=73.1223 CenterY=-32.291 CenterZ=0 NormalX=0 NormalY=0 NormalZ=1 AngleXU=0 Radius=13 StartAngle=5.92268 EndAngle=9.06428
    g2: ArcOfCircle CenterX=66.7816 CenterY=-49.1439 CenterZ=0 NormalX=0 NormalY=0 NormalZ=1 AngleXU=0 Radius=13 StartAngle=2.78068 EndAngle=5.92131
    g3: ArcOfCircle CenterX=55.9263 CenterY=-78.1807 CenterZ=0 NormalX=0 NormalY=0 NormalZ=1 AngleXU=0 Radius=13 StartAngle=5.92268 EndAngle=9.06428
    g4: ArcOfCircle CenterX=49.5884 CenterY=-95.0342 CenterZ=0 NormalX=0 NormalY=0 NormalZ=1 AngleXU=0 Radius=13 StartAngle=2.78068 EndAngle=5.92131
    g5: ArcOfCircle CenterX=38.7206 CenterY=-124.067 CenterZ=0 NormalX=0 NormalY=0 NormalZ=1 AngleXU=0 Radius=13 StartAngle=5.92268 EndAngle=9.06428
    g6: ArcOfCircle CenterX=32.3875 CenterY=-140.92 CenterZ=0 NormalX=0 NormalY=0 NormalZ=1 AngleXU=0 Radius=13 StartAngle=2.78068 EndAngle=5.92131
    g7: ArcOfCircle CenterX=21.4715 CenterY=-169.934 CenterZ=0 NormalX=0 NormalY=0 NormalZ=1 AngleXU=0 Radius=13 StartAngle=5.92268 EndAngle=9.06428
    g8: ArcOfCircle CenterX=15.1336 CenterY=-186.787 CenterZ=0 NormalX=0 NormalY=0 NormalZ=1 AngleXU=0 Radius=13 StartAngle=2.78068 EndAngle=5.92131
    g9-g12: Circle x4 (B-spline internal-alignment scaffolding for g13; pole/knot coordinates omitted)
    g13: BSplineCurve PolesCount=4 KnotsCount=2 Degree=3 IsPeriodic=0
    g14: GeomPoint X=28.8094 Y=-19.0875 Z=0
    g15: GeomPoint X=47.0443 Y=-50.4712 Z=0
    g16: Circle CenterX=53.5586 CenterY=-23.2695 CenterZ=0 NormalX=0 NormalY=0 NormalZ=1 AngleXU=0 Radius=3.24518
    g17: Circle CenterX=-195.441 CenterY=-127.082 CenterZ=0 NormalX=0 NormalY=0 NormalZ=1 AngleXU=0 Radius=1
    g18: Circle CenterX=-8.24091 CenterY=-197.481 CenterZ=0 NormalX=0 NormalY=0 NormalZ=1 AngleXU=0 Radius=1
    g19: Circle CenterX=12.8789 CenterY=-141.321 CenterZ=0 NormalX=0 NormalY=0 NormalZ=1 AngleXU=0 Radius=1
    g20: BSplineCurve PolesCount=3 KnotsCount=2 Degree=2 IsPeriodic=0
    g21: GeomPoint X=-195.441 Y=-127.082 Z=0
    g22: GeomPoint X=12.8789 Y=-141.321 Z=0
    g23: Circle CenterX=-12.8016 CenterY=-179.036 CenterZ=0 NormalX=0 NormalY=0 NormalZ=1 AngleXU=0 Radius=10.5072
    g24: Circle CenterX=0.933922 CenterY=-166.43 CenterZ=0 NormalX=0 NormalY=0 NormalZ=1 AngleXU=0 Radius=3.26661
    g25: Circle CenterX=-33.5518 CenterY=-176.44 CenterZ=0 NormalX=0 NormalY=0 NormalZ=1 AngleXU=0 Radius=5.64388
    g26: Circle CenterX=-47.2366 CenterY=-173.859 CenterZ=0 NormalX=0 NormalY=0 NormalZ=1 AngleXU=0 Radius=3.01653
    g27: Circle CenterX=-56.2595 CenterY=-171.456 CenterZ=0 NormalX=0 NormalY=0 NormalZ=1 AngleXU=0 Radius=2.12826
    g28: ArcOfCircle CenterX=51.2151 CenterY=-198.473 CenterZ=0 NormalX=0 NormalY=0 NormalZ=1 AngleXU=0 Radius=20 StartAngle=2.78189 EndAngle=4.35269
    g29: LineSegment StartX=32.4951 StartY=-191.433 StartZ=0 EndX=94.6578 EndY=-26.1352 EndZ=0
    g30: LineSegment StartX=43.1192 StartY=-220.001 StartZ=0 EndX=-196.497 EndY=-129.89 EndZ=0
    g31: LineSegment StartX=43.1192 StartY=-220.001 StartZ=0 EndX=44.1752 EndY=-217.193 EndZ=0
    g32: LineSegment StartX=117.223 StartY=-19.0875 StartZ=0 EndX=117.223 EndY=-16.0875 EndZ=0
    g33: LineSegment StartX=117.223 StartY=-16.0875 StartZ=0 EndX=17.2232 EndY=-16.0875 EndZ=0
    g34: LineSegment StartX=17.2232 StartY=-16.0875 StartZ=0 EndX=17.2232 EndY=-19.0875 EndZ=0
    g35: LineSegment StartX=28.8094 StartY=-19.0875 StartZ=0 EndX=17.2232 EndY=-19.0875 EndZ=0
    g36: LineSegment StartX=47.0443 StartY=-50.4712 StartZ=0 EndX=12.8789 EndY=-141.321 EndZ=0
    g37: LineSegment StartX=-195.441 StartY=-127.082 StartZ=0 EndX=-196.497 EndY=-129.89 EndZ=0
    g38: LineSegment StartX=85.2866 StartY=-36.8766 StartZ=0 EndX=78.9396 EndY=-53.7463 EndZ=0
    g39: LineSegment StartX=60.9579 StartY=-27.7053 StartZ=0 EndX=54.6191 EndY=-44.5532 EndZ=0
    g40: LineSegment StartX=68.0907 StartY=-82.7664 StartZ=0 EndX=61.7465 EndY=-99.6365 EndZ=0
    g41: LineSegment StartX=43.7619 StartY=-73.595 StartZ=0 EndX=37.426 EndY=-90.4435 EndZ=0
    g42: LineSegment StartX=50.885 StartY=-128.652 StartZ=0 EndX=44.5456 EndY=-145.522 EndZ=0
    g43: LineSegment StartX=26.5562 StartY=-119.481 StartZ=0 EndX=20.2251 EndY=-136.329 EndZ=0
    g44: LineSegment StartX=9.3071 StartY=-165.349 StartZ=0 EndX=2.97115 EndY=-182.197 EndZ=0
    g45: LineSegment StartX=33.6358 StartY=-174.52 StartZ=0 EndX=27.2917 EndY=-191.39 EndZ=0
  constraints (71):
    c: Block(g0)
    c: Block(g1)
    c: Block(g2)
    c: Block(g4)
    c: Block(g3)
    c: Block(g6)
    c: Block(g5)
    c: Block(g8)
    c: Block(g7)
    c: Weight(g9) = 1
    c: Equal(g9,g10)
    c: Equal(g9,g11)
    c: Equal(g9,g12)
    c: InternalAlignment(g9-g12 -> g13) x4
    c: InternalAlignment(g14,g13)
    c: InternalAlignment(g15,g13)
    c: Block(g16)
    c: Weight(g17) = 1
    c: Equal(g17,g18)
    c: Equal(g17,g19)
    c: InternalAlignment(g17,g20)
    c: InternalAlignment(g18,g20)
    c: InternalAlignment(g19,g20)
    c: InternalAlignment(g21,g20)
    c: InternalAlignment(g22,g20)
    c: Block(g20)
    c: Block(g23)
    c: Block(g24)
    c: Block(g25)
    c: Block(g26)
    c: Block(g27)
    c: Block(g28)
    c: Coincident(g29,g28)
    c: Coincident(g29,g0)
    c: Block(g13)
    c: Coincident(g31,g30)
    c: Coincident(g31,g28)
    c: Block(g31)
    c: Coincident(g32,g0)
    c: Vertical(g32)
    c: Coincident(g33,g32)
    c: Horizontal(g33)
    c: Coincident(g34,g33)
    c: Vertical(g34)
    c: Block(g33)
    c: Coincident(g35,g13)
    c: Coincident(g35,g34)
    c: Horizontal(g35)
    c: Coincident(g36,g13)
    c: Coincident(g36,g20)
    c: Coincident(g37,g20)
    c: Coincident(g37,g30)
    c: Block(g30)
    c: Coincident(g38,g1)
    c: Coincident(g38,g2)
    c: Coincident(g39,g1)
    c: Coincident(g39,g2)
    c: Coincident(g40,g3)
    c: Coincident(g40,g4)
    c: Coincident(g41,g3)
    c: Coincident(g41,g4)
    c: Coincident(g42,g5)
    c: Coincident(g42,g6)
    c: Coincident(g43,g5)
    c: Coincident(g43,g6)
    c: Coincident(g44,g7)
    c: Coincident(g44,g8)
    c: Coincident(g45,g7)
    c: Coincident(g45,g8)
    c: Distance(g30) = 256
    c: Distance(g33) = 100
FEATURE [Part::Extrusion] Extrude002
  Base = -> Sketch001
  Dir = (1,0,0)
  DirMode = 2
  FaceMakerClass = Part::FaceMakerBullseye
  LengthFwd = 8
  LengthRev = 0
  Solid = true
  Symmetric = false
FEATURE [Sketcher::SketchObject] Sketch002
  FullyConstrained = true
  sketch-geometry (20):
    g0: LineSegment StartX=-2.77179 StartY=-200.304 StartZ=0 EndX=5.22821 EndY=-200.304 EndZ=0
    g1: LineSegment StartX=5.22821 StartY=-200.304 StartZ=0 EndX=5.22821 EndY=-197.304 EndZ=0
    g2: LineSegment StartX=-2.77179 StartY=-200.304 StartZ=0 EndX=-2.77179 EndY=-197.304 EndZ=0
    g3: LineSegment StartX=5.22821 StartY=-197.304 StartZ=0 EndX=8.22821 EndY=-197.304 EndZ=0
    g4: LineSegment StartX=-2.77179 StartY=-197.304 StartZ=0 EndX=-5.77179 EndY=-197.304 EndZ=0
    g5: LineSegment StartX=19.2282 StartY=-203.304 StartZ=0 EndX=19.2282 EndY=-206.304 EndZ=0
    g6: LineSegment StartX=-16.7718 StartY=-203.304 StartZ=0 EndX=-16.7718 EndY=-206.304 EndZ=0
    g7: LineSegment StartX=-16.7718 StartY=-206.304 StartZ=0 EndX=19.2282 EndY=-206.304 EndZ=0
    g8: Circle CenterX=-16.7718 CenterY=-203.304 CenterZ=0 NormalX=0 NormalY=0 NormalZ=1 AngleXU=0 Radius=1
    g9: Circle CenterX=-5.77179 CenterY=-203.304 CenterZ=0 NormalX=0 NormalY=0 NormalZ=1 AngleXU=0 Radius=1
    g10: Circle CenterX=-5.77179 CenterY=-197.304 CenterZ=0 NormalX=0 NormalY=0 NormalZ=1 AngleXU=0 Radius=1
    g11: BSplineCurve PolesCount=3 KnotsCount=2 Degree=2 IsPeriodic=0
    g12: GeomPoint X=-16.7718 Y=-203.304 Z=0
    g13: GeomPoint X=-5.77179 Y=-197.304 Z=0
    g14: Circle CenterX=19.2282 CenterY=-203.304 CenterZ=0 NormalX=0 NormalY=0 NormalZ=1 AngleXU=0 Radius=1
    g15: Circle CenterX=8.22821 CenterY=-203.304 CenterZ=0 NormalX=0 NormalY=0 NormalZ=1 AngleXU=0 Radius=1
    g16: Circle CenterX=8.22821 CenterY=-197.304 CenterZ=0 NormalX=0 NormalY=0 NormalZ=1 AngleXU=0 Radius=1
    g17: BSplineCurve PolesCount=3 KnotsCount=2 Degree=2 IsPeriodic=0
    g18: GeomPoint X=19.2282 Y=-203.304 Z=0
    g19: GeomPoint X=8.22821 Y=-197.304 Z=0
  constraints (41):
    c: Horizontal(g0)
    c: Distance(g0) = 8
    c: Coincident(g1,g0)
    c: Vertical(g1)
    c: Distance(g1) = 3
    c: Coincident(g2,g0)
    c: Vertical(g2)
    c: Distance(g2) = 3
    c: Coincident(g3,g1)
    c: Horizontal(g3)
    c: Distance(g3) = 3
    c: Coincident(g4,g2)
    c: Horizontal(g4)
    c: Distance(g4) = 3
    c: Vertical(g5)
    c: Vertical(g6)
    c: Coincident(g7,g6)
    c: Coincident(g7,g5)
    c: Weight(g8) = 1
    c: Equal(g8,g9)
    c: Equal(g8,g10)
    c: Coincident(g11,g4)
    c: InternalAlignment(g8,g11)
    c: InternalAlignment(g9,g11)
    c: InternalAlignment(g10,g11)
    c: InternalAlignment(g12,g11)
    c: InternalAlignment(g13,g11)
    c: Coincident(g17,g5)
    c: Weight(g14) = 1
    c: Equal(g14,g15)
    c: Equal(g14,g16)
    c: Coincident(g17,g3)
    c: InternalAlignment(g14,g17)
    c: InternalAlignment(g15,g17)
    c: InternalAlignment(g16,g17)
    c: InternalAlignment(g18,g17)
    c: InternalAlignment(g19,g17)
    c: Block(g7)
    c: Block(g17)
    c: Block(g11)
    c: Block(g6)
FEATURE [Part::Extrusion] Extrude003
  Base = -> Sketch002
  Dir = (0,0,1)
  DirMode = 2
  FaceMakerClass = Part::FaceMakerBullseye
  LengthFwd = 260
  LengthRev = 0
  Solid = true
  Symmetric = false
FEATURE [Part::Extrusion] Extrude
  Base = -> Sketch
  Dir = (0,0,1)
  DirMode = 2
  FaceMakerClass = Part::FaceMakerBullseye
  LengthFwd = 14
  LengthRev = 0
  Solid = true
  Symmetric = false
